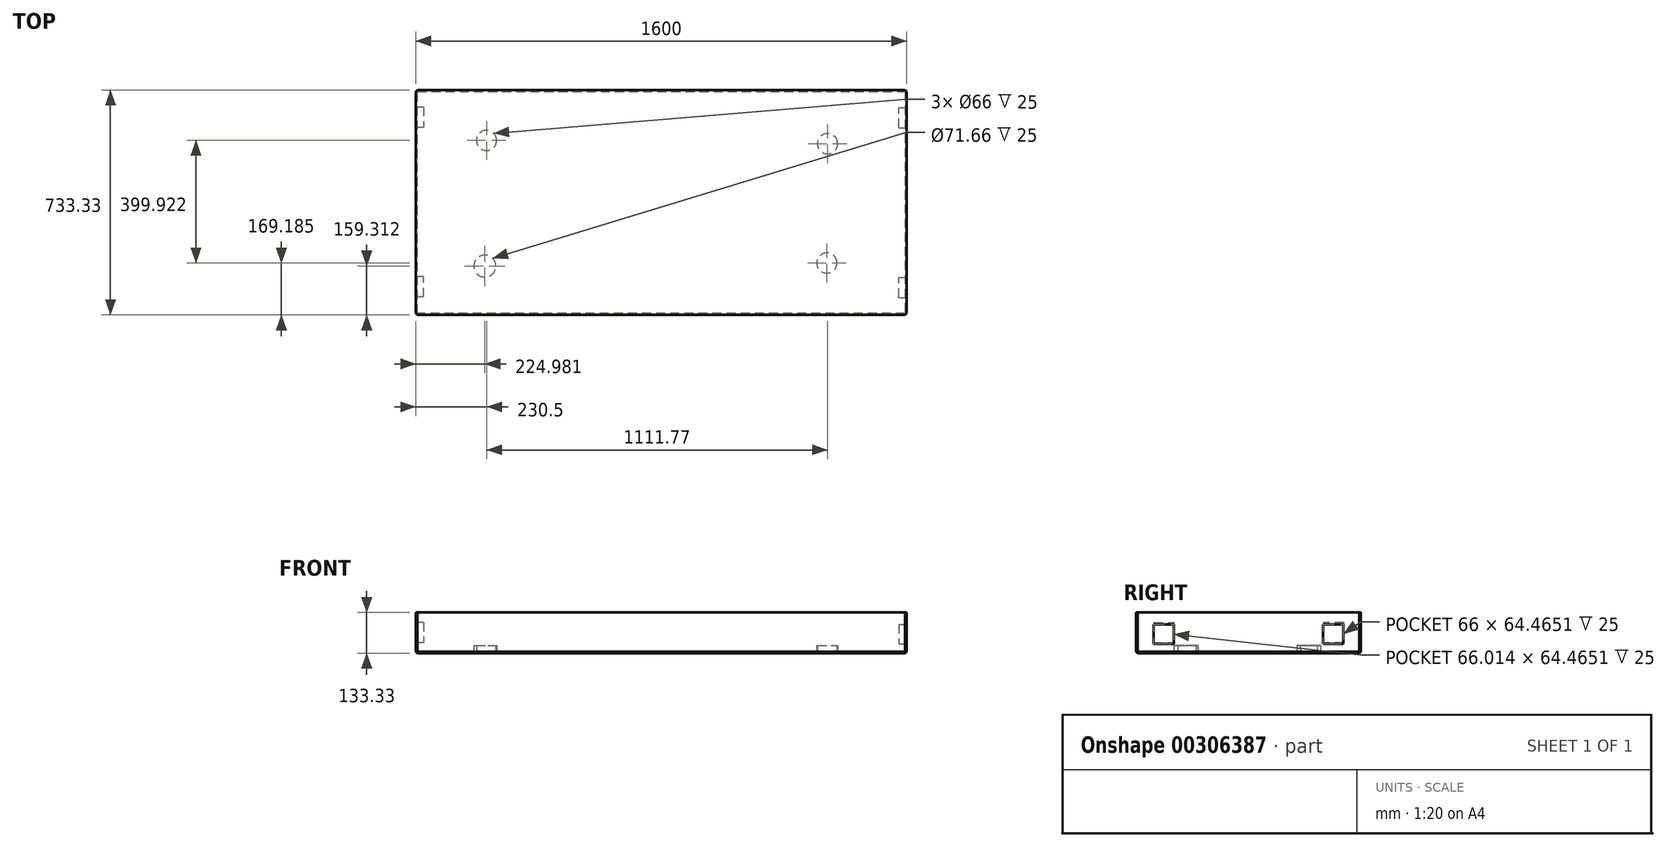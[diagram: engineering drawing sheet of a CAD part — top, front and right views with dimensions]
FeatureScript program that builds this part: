
annotation { "Feature Type Name" : "Feature", "Feature Type Description" : "" }
export const myFeature = defineFeature(function(context is Context, id is Id, definition is map)
    precondition{}
    {
        {
            var Q0;
            Q0=qCreatedBy(makeId("Front.planeOp"),FACE);
            var sketch = newSketch(context, id + "F0", { "sketchPlane" : qUnion([Q0])});
            skLineSegment(sketch, "E0.bottom", {"start": v(-510.48, 0) * mm, "end": v(1089.52, 0) * mm});
            skLineSegment(sketch, "E0.top", {"start": v(-510.48, -133.33) * mm, "end": v(1089.52, -133.33) * mm});
            skLineSegment(sketch, "E0.left", {"start": v(-510.48, 0) * mm, "end": v(-510.48, -133.33) * mm});
            skLineSegment(sketch, "E0.right", {"start": v(1089.52, 0) * mm, "end": v(1089.52, -133.33) * mm});
            skSolve(sketch);
        }
        {
            var Q0;
            Q0=makeQuery(id+"F0.imprint","IMPRINT",FACE,{"disambiguationData":[TD([[makeQuery(id+"F0.imprint","IMPRINT",EDGE,{"derivedFrom":sQuery(id+"F0.wireOp",EDGE,"E0.bottom")}),-1.0]])]});
            extrude(context, id + "F1", {"entities" : qUnion([Q0]), "depth" : 733.33 * mm});
        }
        {
            var Q0;
            Q0=makeQuery(id+"F1.opExtrude","SWEPT_FACE",FACE,{"disambiguationData":[OSD([sQuery(id+"F0.wireOp",EDGE,"E0.left")])]});
            var sketch = newSketch(context, id + "F2", { "sketchPlane" : qUnion([Q0])});
            skLineSegment(sketch, "E1.bottom", {"start": v(674.95, -98.72) * mm, "end": v(608.94, -98.72) * mm});
            skLineSegment(sketch, "E1.top", {"start": v(674.95, -32.7) * mm, "end": v(608.94, -32.7) * mm});
            skLineSegment(sketch, "E1.left", {"start": v(674.95, -98.72) * mm, "end": v(674.95, -32.7) * mm});
            skLineSegment(sketch, "E1.right", {"start": v(608.94, -98.72) * mm, "end": v(608.94, -32.7) * mm});
            skPoint(sketch, "E1.middle", {"position": v(641.95, -65.71) * mm});
            skLineSegment(sketch, "E2.bottom", {"start": v(55.68, -32.7) * mm, "end": v(121.7, -32.7) * mm});
            skLineSegment(sketch, "E2.top", {"start": v(55.68, -98.72) * mm, "end": v(121.7, -98.72) * mm});
            skLineSegment(sketch, "E2.left", {"start": v(55.68, -32.7) * mm, "end": v(55.68, -98.72) * mm});
            skLineSegment(sketch, "E2.right", {"start": v(121.7, -32.7) * mm, "end": v(121.7, -98.72) * mm});
            skPoint(sketch, "E2.middle", {"position": v(88.69, -65.71) * mm});
            skSolve(sketch);
        }
        {
            var Q0;
            Q0=makeQuery(id+"F2.imprint","IMPRINT",FACE,{"disambiguationData":[TD([[makeQuery(id+"F2.imprint","IMPRINT",EDGE,{"derivedFrom":sQuery(id+"F2.wireOp",EDGE,"E1.bottom")}),-1.0]])]});
            var Q1;
            Q1=makeQuery(id+"F2.imprint","IMPRINT",FACE,{"disambiguationData":[TD([[makeQuery(id+"F2.imprint","IMPRINT",EDGE,{"derivedFrom":sQuery(id+"F2.wireOp",EDGE,"E2.bottom")}),-1.0]])]});
            extrude(context, id + "F3", {"entities" : qUnion([Q0, Q1]), "operationType" : NewBodyOperationType.REMOVE, "oppositeDirection" : true, "depth" : 25 * mm});
        }
        {
            var Q0;
            Q0=makeQuery(id+"F1.opExtrude","SWEPT_FACE",FACE,{"disambiguationData":[OSD([sQuery(id+"F0.wireOp",EDGE,"E0.right")])]});
            var sketch = newSketch(context, id + "F4", { "sketchPlane" : qUnion([Q0])});
            skLineSegment(sketch, "E3.bottom", {"start": v(-123.26, -38.98) * mm, "end": v(-57.26, -38.98) * mm});
            skLineSegment(sketch, "E3.top", {"start": v(-123.26, -103.44) * mm, "end": v(-57.26, -103.44) * mm});
            skLineSegment(sketch, "E3.left", {"start": v(-123.26, -38.98) * mm, "end": v(-123.26, -103.44) * mm});
            skLineSegment(sketch, "E3.right", {"start": v(-57.26, -38.98) * mm, "end": v(-57.26, -103.44) * mm});
            skPoint(sketch, "E3.middle", {"position": v(-90.26, -71.21) * mm});
            skLineSegment(sketch, "E4.bottom", {"start": v(-676.53, -38.98) * mm, "end": v(-610.51, -38.98) * mm});
            skLineSegment(sketch, "E4.top", {"start": v(-676.53, -103.44) * mm, "end": v(-610.51, -103.44) * mm});
            skLineSegment(sketch, "E4.left", {"start": v(-676.53, -38.98) * mm, "end": v(-676.53, -103.44) * mm});
            skLineSegment(sketch, "E4.right", {"start": v(-610.51, -38.98) * mm, "end": v(-610.51, -103.44) * mm});
            skPoint(sketch, "E4.middle", {"position": v(-643.52, -71.21) * mm});
            skPoint(sketch, "E4.cornerSnap0", {"position": v(-90.26, -38.98) * mm});
            skSolve(sketch);
        }
        {
            var Q0;
            Q0=makeQuery(id+"F4.imprint","IMPRINT",FACE,{"disambiguationData":[TD([[makeQuery(id+"F4.imprint","IMPRINT",EDGE,{"derivedFrom":sQuery(id+"F4.wireOp",EDGE,"E4.bottom")}),-1.0]])]});
            var Q1;
            Q1=makeQuery(id+"F4.imprint","IMPRINT",FACE,{"disambiguationData":[TD([[makeQuery(id+"F4.imprint","IMPRINT",EDGE,{"derivedFrom":sQuery(id+"F4.wireOp",EDGE,"E3.bottom")}),-1.0]])]});
            extrude(context, id + "F5", {"entities" : qUnion([Q0, Q1]), "operationType" : NewBodyOperationType.REMOVE, "oppositeDirection" : true, "depth" : 25 * mm});
        }
        {
            var Q0;
            Q0=makeQuery(id+"F1.opExtrude","SWEPT_FACE",FACE,{"disambiguationData":[OSD([sQuery(id+"F0.wireOp",EDGE,"E0.top")])]});
            var sketch = newSketch(context, id + "F6", { "sketchPlane" : qUnion([Q0])});
            skCircle(sketch, "E5", {"center": v(829.66, 564.15) * mm, "radius": 33 * mm});
            skCircle(sketch, "E6", {"center": v(831.79, 175.15) * mm, "radius": 33 * mm});
            skCircle(sketch, "E7", {"center": v(-285.5, 574.02) * mm, "radius": 35.83 * mm});
            skCircle(sketch, "E8", {"center": v(-279.98, 164.22) * mm, "radius": 33 * mm});
            skSolve(sketch);
        }
        {
            var Q0;
            Q0=makeQuery(id+"F6.imprint","IMPRINT",FACE,{"disambiguationData":[TD([[makeQuery(id+"F6.imprint","IMPRINT",EDGE,{"derivedFrom":sQuery(id+"F6.wireOp",EDGE,"E5")}),1.0]])]});
            var Q1;
            Q1=makeQuery(id+"F6.imprint","IMPRINT",FACE,{"disambiguationData":[TD([[makeQuery(id+"F6.imprint","IMPRINT",EDGE,{"derivedFrom":sQuery(id+"F6.wireOp",EDGE,"E6")}),1.0]])]});
            var Q2;
            Q2=makeQuery(id+"F6.imprint","IMPRINT",FACE,{"disambiguationData":[TD([[makeQuery(id+"F6.imprint","IMPRINT",EDGE,{"derivedFrom":sQuery(id+"F6.wireOp",EDGE,"E8")}),1.0]])]});
            var Q3;
            Q3=makeQuery(id+"F6.imprint","IMPRINT",FACE,{"disambiguationData":[TD([[makeQuery(id+"F6.imprint","IMPRINT",EDGE,{"derivedFrom":sQuery(id+"F6.wireOp",EDGE,"E7")}),1.0]])]});
            extrude(context, id + "F7", {"entities" : qUnion([Q0, Q1, Q2, Q3]), "operationType" : NewBodyOperationType.REMOVE, "oppositeDirection" : true, "depth" : 25 * mm});
        }
        {
            var Q0;
            Q0=makeQuery(id+"F1.opExtrude","CAP_EDGE",EDGE,{"disambiguationData":[OSD([sQuery(id+"F0.wireOp",EDGE,"E0.top")])],"isStart":false});
            var Q1;
            Q1=makeQuery(id+"F1.opExtrude","CAP_EDGE",EDGE,{"disambiguationData":[OSD([sQuery(id+"F0.wireOp",EDGE,"E0.right")])],"isStart":false});
            var Q2;
            Q2=makeQuery(id+"F1.opExtrude","SWEPT_EDGE",EDGE,{"disambiguationData":[OSD([sQuery(id+"F0.wireOp",EDGE,"E0.top"),sQuery(id+"F0.wireOp",EDGE,"E0.right")])]});
            var Q3;
            Q3=makeQuery(id+"F1.opExtrude","CAP_EDGE",EDGE,{"disambiguationData":[OSD([sQuery(id+"F0.wireOp",EDGE,"E0.right")])],"isStart":true});
            var Q4;
            Q4=makeQuery(id+"F1.opExtrude","CAP_EDGE",EDGE,{"disambiguationData":[OSD([sQuery(id+"F0.wireOp",EDGE,"E0.top")])],"isStart":true});
            var Q5;
            Q5=makeQuery(id+"F1.opExtrude","SWEPT_EDGE",EDGE,{"disambiguationData":[OSD([sQuery(id+"F0.wireOp",EDGE,"E0.top"),sQuery(id+"F0.wireOp",EDGE,"E0.left")])]});
            var Q6;
            Q6=makeQuery(id+"F1.opExtrude","CAP_EDGE",EDGE,{"disambiguationData":[OSD([sQuery(id+"F0.wireOp",EDGE,"E0.left")])],"isStart":true});
            var Q7;
            Q7=makeQuery(id+"F1.opExtrude","CAP_EDGE",EDGE,{"disambiguationData":[OSD([sQuery(id+"F0.wireOp",EDGE,"E0.left")])],"isStart":false});
            chamfer(context, id + "F8", {"entities" : qUnion([Q0, Q1, Q2, Q3, Q4, Q5, Q6, Q7]), "width" : 5 * mm, "tangentPropagation" : true});
        }
    });
